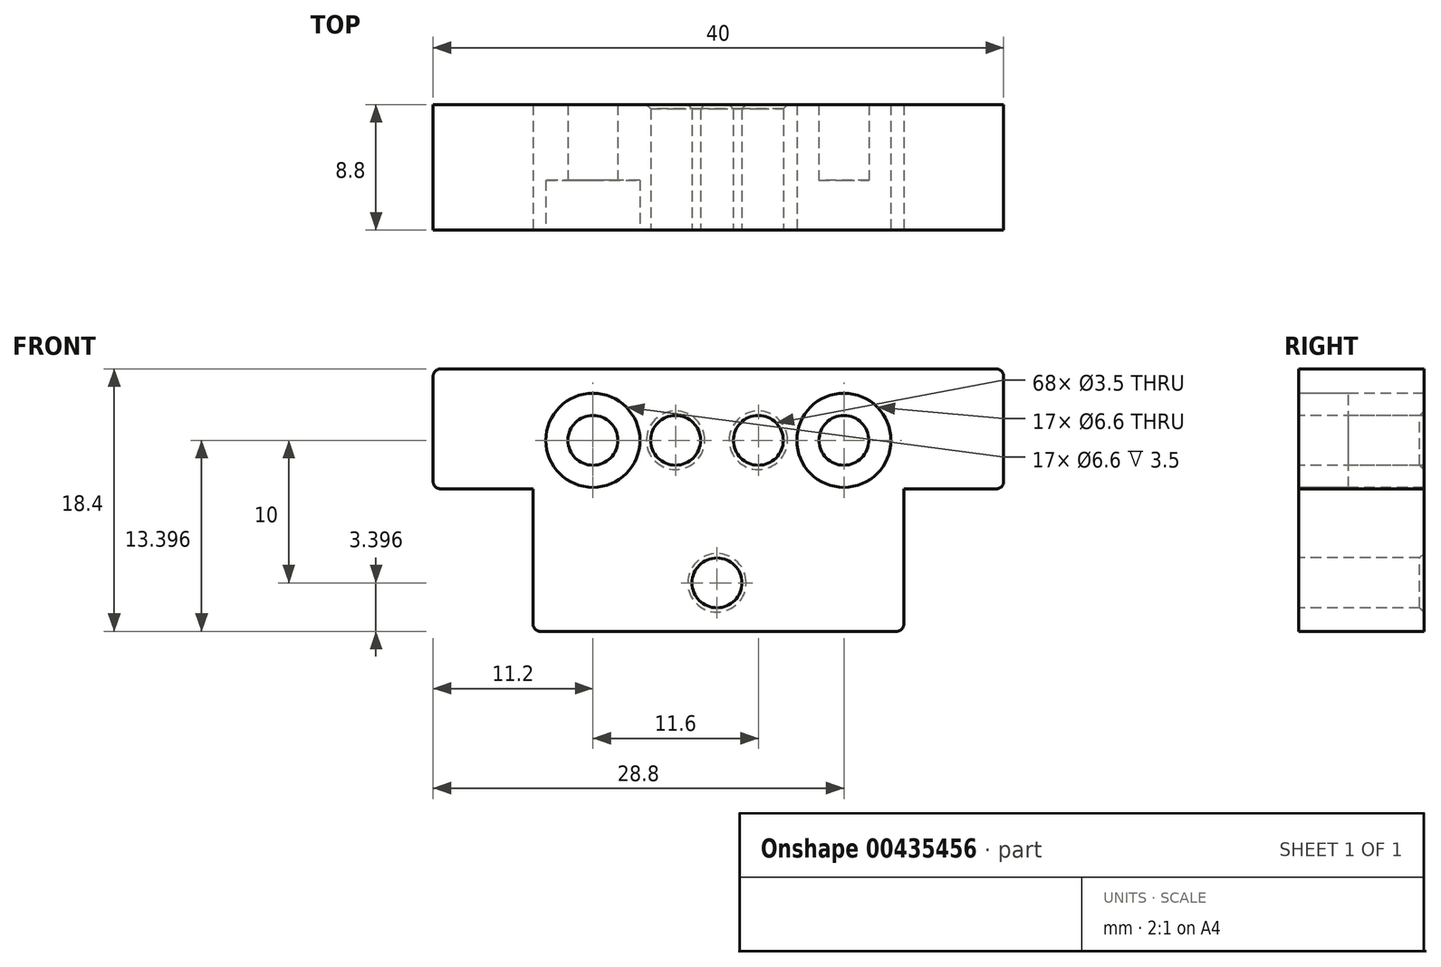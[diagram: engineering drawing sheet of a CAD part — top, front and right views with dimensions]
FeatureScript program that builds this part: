
annotation { "Feature Type Name" : "Feature", "Feature Type Description" : "" }
export const myFeature = defineFeature(function(context is Context, id is Id, definition is map)
    precondition{}
    {
        {
            var Q0;
            Q0=qCreatedBy(makeId("Front.planeOp"),FACE);
            var sketch = newSketch(context, id + "F0", { "sketchPlane" : qUnion([Q0])});
            skLineSegment(sketch, "E0.bottom", {"start": v(-11.2, -3.78) * mm, "end": v(28.8, -3.78) * mm});
            skLineSegment(sketch, "E0.top", {"start": v(-11.2, -12.18) * mm, "end": v(-4.2, -12.18) * mm});
            skLineSegment(sketch, "E0.left", {"start": v(-11.2, -3.78) * mm, "end": v(-11.2, -12.18) * mm});
            skLineSegment(sketch, "E0.right", {"start": v(28.8, -3.78) * mm, "end": v(28.8, -12.18) * mm});
            skLineSegment(sketch, "E1.top", {"start": v(-4.2, -22.18) * mm, "end": v(21.8, -22.18) * mm});
            skLineSegment(sketch, "E1.left", {"start": v(-4.2, -12.18) * mm, "end": v(-4.2, -22.18) * mm});
            skLineSegment(sketch, "E1.right", {"start": v(21.8, -12.18) * mm, "end": v(21.8, -22.18) * mm});
            skCircle(sketch, "E2", {"center": v(0, -8.78) * mm, "radius": 1.75 * mm});
            skCircle(sketch, "E3.MirrorC", {"center": v(17.6, -8.78) * mm, "radius": 1.75 * mm});
            skCircle(sketch, "E4.MirrorC", {"center": v(17.6, -8.78) * mm, "radius": 3.3 * mm});
            skCircle(sketch, "E5.MirrorC", {"center": v(0, -8.78) * mm, "radius": 3.3 * mm});
            skLineSegment(sketch, "E6.trimOffspring", {"start": v(21.8, -12.18) * mm, "end": v(28.8, -12.18) * mm});
            skCircle(sketch, "E7.1.0.0", {"center": v(5.8, -8.78) * mm, "radius": 1.75 * mm});
            skCircle(sketch, "E7.2.0.0", {"center": v(11.6, -8.78) * mm, "radius": 1.75 * mm});
            skLineSegment(sketch, "E7.direction1", {"start": v(0, -8.78) * mm, "end": v(5.8, -8.78) * mm, "construction": true});
            skCircle(sketch, "E8", {"center": v(8.7, -18.78) * mm, "radius": 1.75 * mm});
            skCircle(sketch, "E9", {"center": v(5.8, -8.78) * mm, "radius": 1.95 * mm});
            skCircle(sketch, "E10", {"center": v(11.6, -8.78) * mm, "radius": 1.95 * mm});
            skCircle(sketch, "E11", {"center": v(8.7, -18.78) * mm, "radius": 1.95 * mm});
            skSolve(sketch);
        }
        {
            var Q0;
            Q0=makeQuery(id+"F0.imprint","IMPRINT",FACE,{"disambiguationData":[TD([[makeQuery(id+"F0.imprint","IMPRINT",EDGE,{"derivedFrom":sQuery(id+"F0.wireOp",EDGE,"E0.bottom")}),-1.0]])]});
            var Q1;
            Q1=makeQuery(id+"F0.imprint","IMPRINT",FACE,{"disambiguationData":[TD([[makeQuery(id+"F0.imprint","IMPRINT",EDGE,{"derivedFrom":sQuery(id+"F0.wireOp",EDGE,"E2")}),-1.0]])]});
            var Q2;
            Q2=makeQuery(id+"F0.imprint","IMPRINT",FACE,{"disambiguationData":[TD([[makeQuery(id+"F0.imprint","IMPRINT",EDGE,{"derivedFrom":sQuery(id+"F0.wireOp",EDGE,"E3.MirrorC")}),1.0]])]});
            var Q3;
            Q3=makeQuery(id+"F0.imprint","IMPRINT",FACE,{"disambiguationData":[TD([[makeQuery(id+"F0.imprint","IMPRINT",EDGE,{"derivedFrom":sQuery(id+"F0.wireOp",EDGE,"E7.2.0.0")}),-1.0]])]});
            var Q4;
            Q4=makeQuery(id+"F0.imprint","IMPRINT",FACE,{"disambiguationData":[TD([[makeQuery(id+"F0.imprint","IMPRINT",EDGE,{"derivedFrom":sQuery(id+"F0.wireOp",EDGE,"E7.1.0.0")}),-1.0]])]});
            var Q5;
            Q5=makeQuery(id+"F0.imprint","IMPRINT",FACE,{"disambiguationData":[TD([[makeQuery(id+"F0.imprint","IMPRINT",EDGE,{"derivedFrom":sQuery(id+"F0.wireOp",EDGE,"E8")}),-1.0]])]});
            extrude(context, id + "F1", {"entities" : qUnion([Q0, Q1, Q2, Q3, Q4, Q5]), "oppositeDirection" : true, "depth" : 8.8 * mm});
        }
        {
            var Q0;
            Q0=makeQuery(id+"F0.imprint","IMPRINT",FACE,{"disambiguationData":[TD([[makeQuery(id+"F0.imprint","IMPRINT",EDGE,{"derivedFrom":sQuery(id+"F0.wireOp",EDGE,"E3.MirrorC")}),1.0]])]});
            extrude(context, id + "F2", {"entities" : qUnion([Q0]), "operationType" : NewBodyOperationType.REMOVE, "oppositeDirection" : true, "depth" : 3.5 * mm});
        }
        {
            var Q0;
            Q0=makeQuery(id+"F0.imprint","IMPRINT",FACE,{"disambiguationData":[TD([[makeQuery(id+"F0.imprint","IMPRINT",EDGE,{"derivedFrom":sQuery(id+"F0.wireOp",EDGE,"E2")}),-1.0]])]});
            extrude(context, id + "F3", {"entities" : qUnion([Q0]), "operationType" : NewBodyOperationType.REMOVE, "oppositeDirection" : true, "depth" : 3.5 * mm});
        }
        {
            var Q0;
            Q0=makeQuery(id+"F1.opExtrude","CAP_EDGE",EDGE,{"disambiguationData":[OSD([sQuery(id+"F0.wireOp",EDGE,"E7.2.0.0")])],"isStart":false});
            var Q1;
            Q1=makeQuery(id+"F1.opExtrude","CAP_EDGE",EDGE,{"disambiguationData":[OSD([sQuery(id+"F0.wireOp",EDGE,"E7.1.0.0")])],"isStart":false});
            var Q2;
            Q2=makeQuery(id+"F1.opExtrude","CAP_EDGE",EDGE,{"disambiguationData":[OSD([sQuery(id+"F0.wireOp",EDGE,"E8")])],"isStart":false});
            chamfer(context, id + "F4", {"entities" : qUnion([Q0, Q1, Q2]), "width" : 0.3 * mm, "tangentPropagation" : true});
        }
        {
            var Q0;
            Q0=makeQuery(id+"F1.opExtrude","SWEPT_EDGE",EDGE,{"disambiguationData":[OSD([sQuery(id+"F0.wireOp",EDGE,"E0.bottom"),sQuery(id+"F0.wireOp",EDGE,"E0.left")])]});
            var Q1;
            Q1=makeQuery(id+"F1.opExtrude","SWEPT_EDGE",EDGE,{"disambiguationData":[OSD([sQuery(id+"F0.wireOp",EDGE,"E0.top"),sQuery(id+"F0.wireOp",EDGE,"E0.left")])]});
            var Q2;
            Q2=makeQuery(id+"F1.opExtrude","SWEPT_EDGE",EDGE,{"disambiguationData":[OSD([sQuery(id+"F0.wireOp",EDGE,"E1.top"),sQuery(id+"F0.wireOp",EDGE,"E1.left")])]});
            var Q3;
            Q3=makeQuery(id+"F1.opExtrude","SWEPT_EDGE",EDGE,{"disambiguationData":[OSD([sQuery(id+"F0.wireOp",EDGE,"E0.right"),sQuery(id+"F0.wireOp",EDGE,"E6.trimOffspring")])]});
            var Q4;
            Q4=makeQuery(id+"F1.opExtrude","SWEPT_EDGE",EDGE,{"disambiguationData":[OSD([sQuery(id+"F0.wireOp",EDGE,"E0.bottom"),sQuery(id+"F0.wireOp",EDGE,"E0.right")])]});
            var Q5;
            Q5=makeQuery(id+"F1.opExtrude","SWEPT_EDGE",EDGE,{"disambiguationData":[OSD([sQuery(id+"F0.wireOp",EDGE,"E1.top"),sQuery(id+"F0.wireOp",EDGE,"E1.right")])]});
            fillet(context, id + "F5", {"entities" : qUnion([Q0, Q1, Q2, Q3, Q4, Q5]), "radius" : 0.5 * mm, "tangentPropagation" : true, "allowEdgeOverflow" : false});
        }
    });
